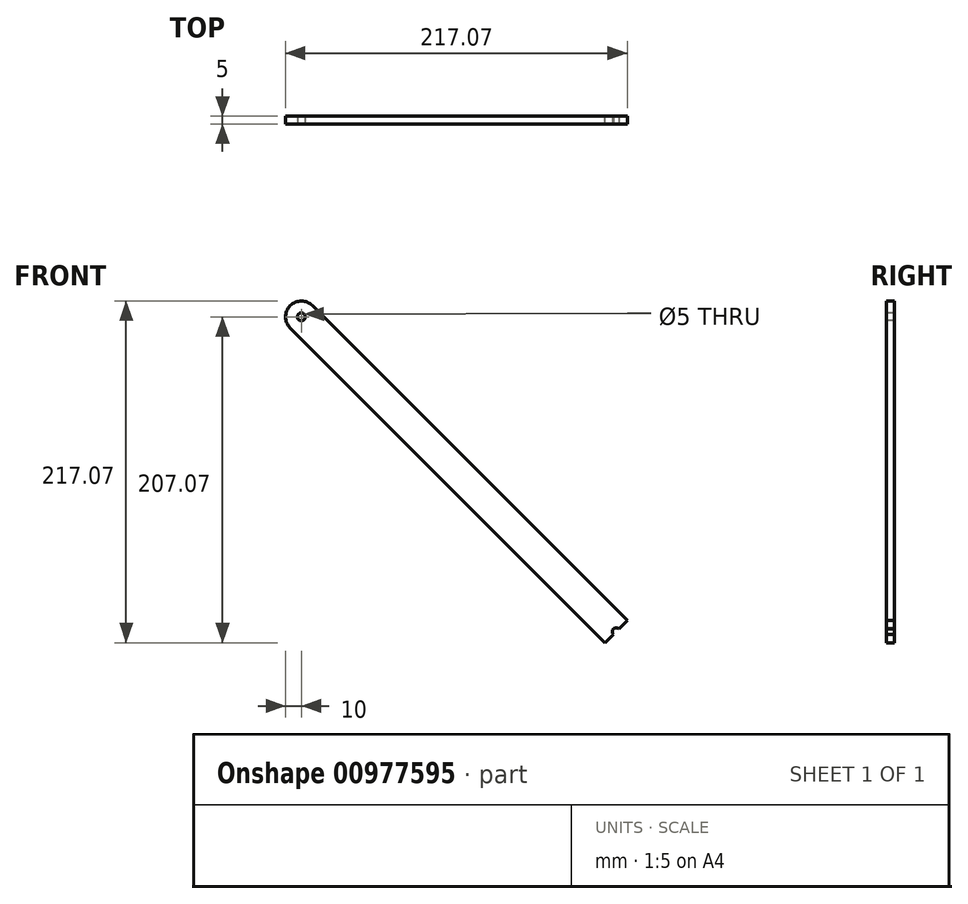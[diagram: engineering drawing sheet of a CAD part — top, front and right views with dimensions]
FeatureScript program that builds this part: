
annotation { "Feature Type Name" : "Feature", "Feature Type Description" : "" }
export const myFeature = defineFeature(function(context is Context, id is Id, definition is map)
    precondition{}
    {
        {
            var Q0;
            Q0=qCreatedBy(makeId("Front.planeOp"),FACE);
            var sketch = newSketch(context, id + "F0", { "sketchPlane" : qUnion([Q0])});
            skLineSegment(sketch, "E0.0", {"start": v(-7.07, -7.07) * mm, "end": v(192.93, -207.07) * mm});
            skLineSegment(sketch, "E1.0", {"start": v(7.07, 7.07) * mm, "end": v(207.07, -192.93) * mm});
            skArc(sketch, "E2", {"start": v(7.07, 7.07) * mm, "mid": v(-7.07, 7.07) * mm, "end": v(-7.07, -7.07) * mm});
            skArc(sketch, "E3", {"start": v(207.07, -192.93) * mm, "mid": v(207.07, -207.07) * mm, "end": v(192.93, -207.07) * mm});
            skLineSegment(sketch, "E4", {"start": v(0, -200) * mm, "end": v(200, -200) * mm, "construction": true});
            skLineSegment(sketch, "E5", {"start": v(7.07, 7.07) * mm, "end": v(-7.07, -7.07) * mm});
            skLineSegment(sketch, "E6", {"start": v(207.07, -192.93) * mm, "end": v(192.93, -207.07) * mm});
            skSolve(sketch);
        }
        {
            var Q0;
            Q0=makeQuery(id+"F0.imprint","IMPRINT",FACE,{"disambiguationData":[TD([[makeQuery(id+"F0.imprint","IMPRINT",EDGE,{"derivedFrom":sQuery(id+"F0.wireOp",EDGE,"E2")}),1.0]])]});
            var Q1;
            Q1=makeQuery(id+"F0.imprint","IMPRINT",FACE,{"disambiguationData":[TD([[makeQuery(id+"F0.imprint","IMPRINT",EDGE,{"derivedFrom":sQuery(id+"F0.wireOp",EDGE,"E0.0")}),1.0]])]});
            var Q2;
            Q2=makeQuery(id+"F0.imprint","IMPRINT",FACE,{"disambiguationData":[TD([[makeQuery(id+"F0.imprint","IMPRINT",EDGE,{"derivedFrom":sQuery(id+"F0.wireOp",EDGE,"E3")}),-1.0]])]});
            extrude(context, id + "F1", {"entities" : qUnion([Q0, Q1, Q2]), "depth" : 5 * mm, "offsetDistance" : 25 * mm});
        }
        {
            var Q0;
            Q0=makeQuery(id+"F1.opExtrude","CAP_FACE",FACE,{"disambiguationData":[OSD([sQuery(id+"F0.wireOp",EDGE,"E0.0"),sQuery(id+"F0.wireOp",EDGE,"E1.0"),sQuery(id+"F0.wireOp",EDGE,"E2"),sQuery(id+"F0.wireOp",EDGE,"E3")])],"isStart":false});
            var sketch = newSketch(context, id + "F2", { "sketchPlane" : qUnion([Q0])});
            skCircle(sketch, "E7", {"center": v(0, 0) * mm, "radius": 2.5 * mm});
            skSolve(sketch);
        }
        {
            var Q0;
            Q0 = qSketchRegion(id + "F2", true);
            extrude(context, id + "F3", {"entities" : qUnion([Q0]), "operationType" : NewBodyOperationType.REMOVE, "oppositeDirection" : true, "depth" : 25 * mm, "offsetDistance" : 25 * mm});
        }
        {
            var Q0;
            Q0=makeQuery(id+"F1.opExtrude","CAP_FACE",FACE,{"disambiguationData":[OSD([sQuery(id+"F0.wireOp",EDGE,"E0.0"),sQuery(id+"F0.wireOp",EDGE,"E1.0"),sQuery(id+"F0.wireOp",EDGE,"E2"),sQuery(id+"F0.wireOp",EDGE,"E3")])],"isStart":false});
            var sketch = newSketch(context, id + "F4", { "sketchPlane" : qUnion([Q0])});
            skCircle(sketch, "E8", {"center": v(200, -200) * mm, "radius": 2.5 * mm});
            skSolve(sketch);
        }
        {
            var Q0;
            Q0=makeQuery(id+"F4.imprint","IMPRINT",FACE,{"disambiguationData":[TD([[makeQuery(id+"F4.imprint","IMPRINT",EDGE,{"derivedFrom":sQuery(id+"F4.wireOp",EDGE,"E8")}),1.0]])]});
            extrude(context, id + "F5", {"entities" : qUnion([Q0]), "operationType" : NewBodyOperationType.REMOVE, "oppositeDirection" : true, "depth" : 25 * mm, "offsetDistance" : 25 * mm});
        }
    });
